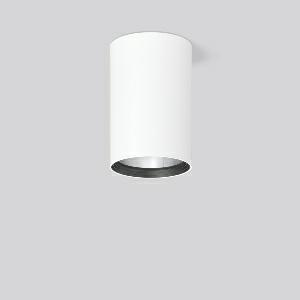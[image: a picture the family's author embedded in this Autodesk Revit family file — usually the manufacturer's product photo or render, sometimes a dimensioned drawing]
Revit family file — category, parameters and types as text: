
# Revit family: heledon_maxi_a_931218_002_1_76_649a
name_source: partatom
category: Lighting Fixtures
units: mm (PartAtom-declared; Revit-internal decimal feet)

## family parameters
Cut with Voids When Loaded = No
Host = Face
Light Source = No
Part Type = Normal
Room Calculation Point = No
Round Connector Dimension = Use Diameter
Shared = No

## types (1)
- HELEDON maxi A (1 x LED Modul 940, 3500 lm, 4000)
    Apparent Load = 25 VA
    Approval mark = CE
    CIE Flux Codes = 100 100 100 100 100
    Color Rendering = 92
    Color Temperature = 4000
    Default Elevation = 1800 mm
    Description = Series: HELEDON maxi
Cylindrical surface-mounted downlight. Housing: die-cast aluminium, powder-coated. Internal ceiling frame polycarbonate with bayonet mounting. Black plastic ring and recessed LED to prevent glare from the side. Optical assembly with reflector made of MIRO-Silver with 98% total light reflection for outstanding efficiency - can be changed without tools. Best colour rendering index Ra>90. Suitable for Ceiling mounting. Easy installation with a separate ceiling frame with bayonet mounting and plug connection. Driver integrated. Connected via plug-in connector. High quality converter without flickering and stroboscopic effect. The following accessories can be mounted without use of tools: interchangeable lenses, decorative glasses, honeycomb louvre, clear and frosted diffusers, white interchangeable plastic ring. 
Colour: traffic white, matt (RAL 9016)
Diameter: 123 mm
Height: 183 mm
Lamp: LED
Socket: without socket
Colour temperature: 4000K
Colour rendering index (CRI): 92
System power: 25 W
Rated luminous flux: 3500 lm
Luminous efficiency: 140 lm/W
Control gear: Converter, dimmable, DALI
Protection class: I
Type of protection: IP 20
    Height = 183 mm
    Lamp = 1 x LED Modul 940
    Lamp Light Flux = 3500 lm
    Lamp count = 1
    Length = 123 mm
    Lifetime = 50000 h
    Luminous efficacy = 140 lm/W
    Manufacturer = RZB
    ModVariant = No
    Model = 931218.002.1.76
    Mounting Place = Ceiling
    Mounting Type = Surface mounted
    Number of Poles = 1
    OnlyDefault = Yes
    Power Factor = 1
    Product Name = HELEDON maxi A
    Product group = Surface mounted downlights
    ProductGroupID = 302
    Protection Class = Protection class I
    Protection Degree = IP 20
    RLX_Detail_Level = 1
    RLX_Emergency_Light_Flux = 0 lm
    RLX_Emergency_Type = 0
    RLX_Emergency_Type_DB = No
    RlxData = <blob elided: 97377 chars, md5=efab2175>
    Socket = socket
    Standby Power = 0 W
    System Light Flux = 3500 lm
    System Power = 25 W
    Type Comments = Product without accessories
    Type Image = 931192.002.jpg
    URL = http://relux.com
    VarID = ---
    Voltage = 230 V
    Voltage Range = 220-240 V
    Weight = 0.00 kg
    Width = 0 mm  [stored 0 ft]

note: [stored X ft] marks values corroborated as IEEE doubles in the binary element streams (Revit-internal decimal feet)

## geometry (parser evidence)
native form markers: Blend x4, Sweep x10
no freeform markers — native parametric forms only
